# Revit family: Auto-Door_Swing_Tormax_iMotion-1302-Package-Single
name_source: partatom
category: Doors
units: mm (PartAtom-declared; Revit-internal decimal feet)

## family parameters
Always vertical = Yes
Classification Number = 23.30.10.14.24
Cut with Voids When Loaded = No
Host = Wall
Room Calculation Point = No
Shared = No

## types (4) — shared parameters
Air Infiltration = as Specified
Air Space Below Door = 0' - 0 3/16"
Analytic Construction = <None>
Assembly Code = B2030110
Available Options = as Specified
Capacity = Up to 275 lbs or up to 48 inch Wide Panels
Construction Details = https://www.arcat.com
Define Thermal Properties by = Schematic Type
Electrical_Amperage = 5 A
Electrical_Voltage = 120 V
Electrical_Wattage = 250 W
Fire Rating = as Specified
Frame Thickness = 0' - 4 1/2"
Function = Exterior
Green Building-LEED = https://www.arcat.com
Heat Transfer Coefficient (U) = 0.1 BTU/(h·ft²·°F)
Keynote = 08 71 13
Manufacturer = TORMAX USA Inc.
Manufacturer Fax = 210-494-5930
Manufacturer Website = http://www.tormaxusa.com
Miami Dade Conformance = as Specified
Operating Temperature Range = as Specified
Panel Thickness = 0' - 1 3/4"
Product Data = https://www.arcat.com
R = 0.0000 (h·ft²·°F)/BTU
RO Spacing_Sides = 0' - 0 1/4"
RO Spacing_Top = 0' - 0 1/4"
Sales Information = http://www.tormaxusa.com
Send Message = http://www.arcat.com
Sound Pressure = <70 dBA
SpecWizard = https://www.arcat.com
Specification = https://www.arcat.com
Standards Conformance = UL325  ;  ANSI A156.19  ;  ANSI A156.10  ;  ADA
Structural Test Pressure = as Specified
Thermal Resistance (R) = 0.0000 (h·ft²·°F)/BTU
Thickness = 0' - 1 3/4"
U = 0.1 BTU/(h·ft²·°F)
URL = http://www.tormaxusa.com
Wall Closure = By host
Water Penetration = as Specified
zero-valued in all types: Expected Lifespan (Years), Maintenance Schedule (Months), SHGC, Solar Heat Gain Coefficient, VLT, Visual Light Transmittance, Warranty Duration (Years)

## per-type parameters (varying)
| type | Description | Include Transom | Model |
| Tormax Package | Tormax Swing Door with OHC iMotion 1302 Swing Door Operator - Package as Specified | No | iMotion 1302 Package |
| Tormax Package with Transom | Tormax Swing Door with OHC iMotion 1302 Swing Door Operator - Package as Specified | Yes | iMotion 1302 Package |
| Door and Frame by Others | Tormax OHC iMotion 1302 Swing Door Operator - Door Package by Others as Specified | No | iMotion 1302 |
| Door and Frame and Transom by Others | Tormax OHC iMotion 1302 Swing Door Operator - Door Package by Others as Specified | Yes | iMotion 1302 |

## geometry (parser evidence)
native form markers: Blend x4, Sweep x9
no freeform markers — native parametric forms only
